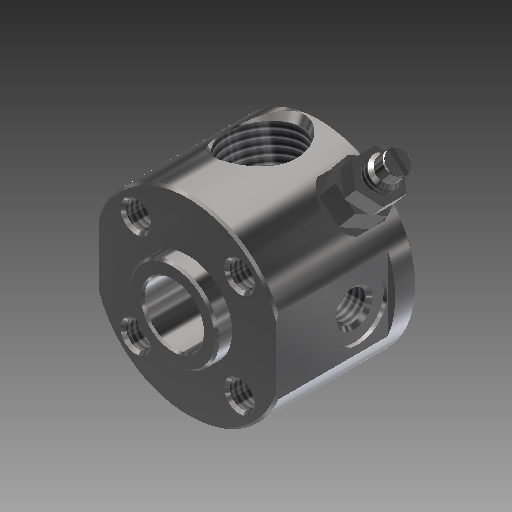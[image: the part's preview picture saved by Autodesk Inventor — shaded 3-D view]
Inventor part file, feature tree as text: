
AUTODESK INVENTOR PART (.ipt)
format: ipt  version: 2018 (Build 220112000, 112)  size: 352,256 bytes
history: native  units: in
note: dims shown in document units (in); Inventor stores cm internally (conversion verified against a paired STEP export)
features: other x42, sketch x14, revolve x5, extrude x5, hole x4, thread x4
ambient origin geometry x8: Origin, YZ Plane, XZ Plane, XY Plane, X Axis, Y Axis, Z Axis, Center Point
bodies: Solid1 (feature_tree)
feature tree (74):
  revolve  "Revolution1"  [1 undecoded]
  hole  "Hole1"  [1 undecoded]
  hole  "Hole2"  [1 undecoded]
  hole  "Hole3"  [1 undecoded]
  hole  "Hole4"  [1 undecoded]
  extrude  "Extrusion1"  Depth=0.252in TaperAngle=0.0deg
  revolve  "Revolution2"  [1 undecoded]
  thread  "Thread1"  [1 undecoded]
  revolve  "Revolution3"  [1 undecoded]
  thread  "Thread2"  [1 undecoded]
  extrude  "Extrusion2"  [1 undecoded]
  extrude  "Extrusion3"  [1 undecoded]
  extrude  "Extrusion4"  [1 undecoded]
  revolve  "Revolution4"  [1 undecoded]
  thread  "Thread3"  [1 undecoded]
  extrude  "Extrusion5"  [1 undecoded]
  revolve  "Revolution5"  [1 undecoded]
  thread  "Thread4"  [1 undecoded]
  other  "conn_XY"
  other  "conn_YZ"
  other  "conn_ZX"
  other  "conn_X"
  other  "conn_Y"
  other  "conn_Z"
  other  "conn_Center"
  other  "conn2_XY"
  other  "conn2_YZ"
  other  "conn2_ZX"
  other  "conn2_X"
  other  "conn2_Y"
  other  "conn2_Z"
  other  "conn2_Center"
  other  "mnt_XY"
  other  "mnt_YZ"
  other  "mnt_ZX"
  other  "mnt_X"
  other  "mnt_Y"
  other  "mnt_Z"
  other  "mnt_Center"
  other  "rod_XY"
  other  "rod_YZ"
  other  "rod_ZX"
  other  "rod_X"
  other  "rod_Y"
  other  "rod_Z"
  other  "rod_Center"
  other  "trun1_XY"
  other  "trun1_YZ"
  other  "trun1_ZX"
  other  "trun1_X"
  other  "trun1_Y"
  other  "trun1_Z"
  other  "trun1_Center"
  other  "trun2_XY"
  other  "trun2_YZ"
  other  "trun2_ZX"
  other  "trun2_X"
  other  "trun2_Y"
  other  "trun2_Z"
  other  "trun2_Center"
  sketch  "Sketch_3"  dims[d1=0.134in d2=0.28in d3=0.164in d4=0.25in d5=90.0deg d6=0.28in d7=0.8383in]
  sketch  "Sketch2"  dims[d0=360.0deg]
  sketch  "Sketch3"  dims[d8=0.134in d9=0.28in d10=0.164in d11=0.25in d12=90.0deg d13=0.28in d14=0.8383in]
  sketch  "Sketch4"  dims[d15=0.134in d16=0.28in d17=0.164in d18=0.25in d19=90.0deg d20=0.28in d21=0.8383in]
  sketch  "Sketch5"  dims[d22=0.134in d23=0.28in d24=0.164in d25=0.25in d26=90.0deg d27=0.28in d28=0.8383in d29=0.5915in d30=0.0in]
  sketch  "Sketch_6"  dims[d31=360.0deg d32=0.1399in d33=0.0in]
  sketch  "Sketch_7"  dims[d34=360.0deg d35=0.1399in d36=0.0in]
  sketch  "Sketch_8"  dims[d37=0.138in d38=0.0in d39=0.138in d40=0.0in]
  sketch  "Sketch_13"
  sketch  "Sketch_14"
  sketch  "Sketch_15"
  sketch  "Sketch_9"  dims[d41=0.094in d42=0.0in d43=360.0deg]
  sketch  "Sketch_11"  dims[d48=360.0deg d49=0.2731in d50=0.0in d51=0.0in d52=0.0in d53=0.0in d54=0.0in]
  sketch  "Sketch_10"  dims[d44=0.0573in d45=0.0in d46=0.252in d47=0.0in]
note: 17 required parameter values undecoded (feature->parameter linkage not recoverable at this tier; creation-order binding heuristic only, values carry confidence <= 0.55)